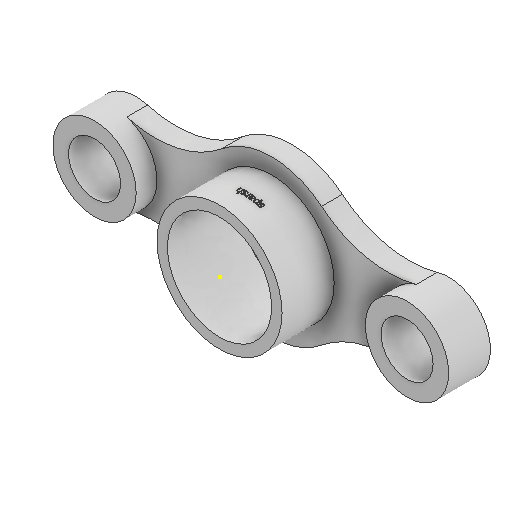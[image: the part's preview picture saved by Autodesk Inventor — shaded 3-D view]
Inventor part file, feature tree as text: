
AUTODESK INVENTOR PART (.ipt)
format: ipt  version: 2025.2 (Build 292293000, 293)  size: 586,240 bytes
history: native  units: in
note: dims shown in document units (in); Inventor stores cm internally (conversion verified against a paired STEP export)
features: sketch x4, extrude x3, plane x2, emboss x1
ambient origin geometry x8: Origin, YZ Plane, XZ Plane, XY Plane, X Axis, Y Axis, Z Axis, Center Point
bodies: Solid1 (feature_tree)
feature tree (10):
  sketch  "Sketch1"  dims[d0=4.7244in d1=3.937in]
  extrude  "Extrusion1"  Depth=3.937in
  extrude  "Extrusion2"  Depth=1.9685in
  extrude  "Extrusion3"  Depth=5.9055in
  sketch  "Sketch2"  dims[d2=5.9055in d3=1.9685in]
  plane  "Work Plane1"
  sketch  "Sketch3"  dims[d4=3.1496in d6=5.9055in]
  plane  "Work Plane2"
  emboss  "Emboss1"
  sketch  "Sketch4"  dims[d8=7.874in d9=3.937in d10=2.7559in d11=0.0in d12=1.5748in d13=0.0in d14=0.7874in d15=0.0in d16=-2.3622in d17=2.3622in d18=0.3937in d19=0.0in]
